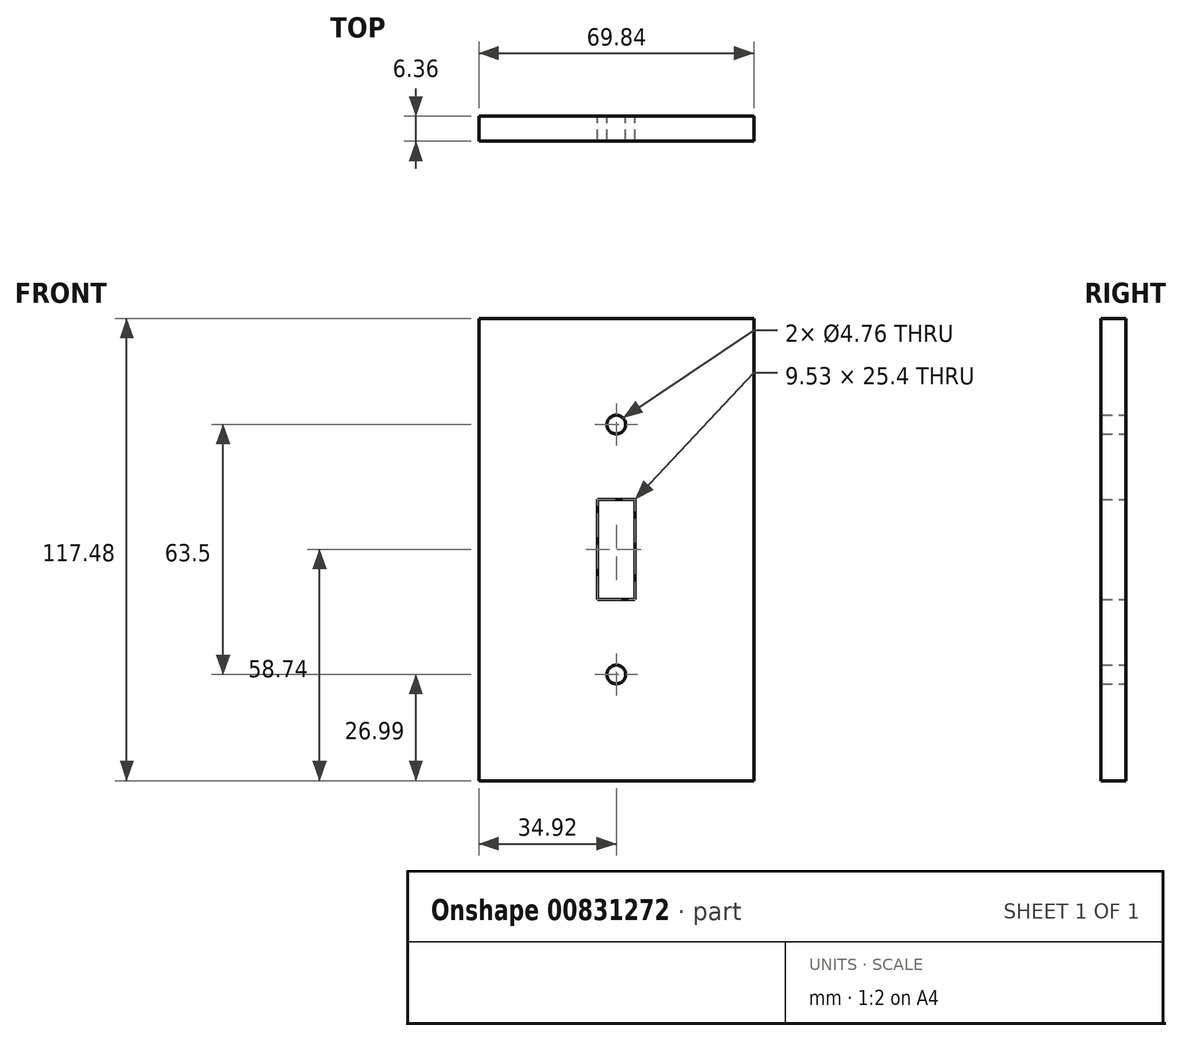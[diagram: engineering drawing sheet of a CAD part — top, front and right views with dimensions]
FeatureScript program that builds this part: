
annotation { "Feature Type Name" : "Feature", "Feature Type Description" : "" }
export const myFeature = defineFeature(function(context is Context, id is Id, definition is map)
    precondition{}
    {
        {
            var Q0;
            Q0=qCreatedBy(makeId("Front.planeOp"),FACE);
            var sketch = newSketch(context, id + "F0", { "sketchPlane" : qUnion([Q0])});
            skLineSegment(sketch, "E0.bottom", {"start": v(-34.92, 58.74) * mm, "end": v(34.93, 58.74) * mm});
            skLineSegment(sketch, "E0.top", {"start": v(-34.93, -58.74) * mm, "end": v(34.92, -58.74) * mm});
            skLineSegment(sketch, "E0.left", {"start": v(-34.92, 58.74) * mm, "end": v(-34.93, -58.74) * mm});
            skLineSegment(sketch, "E0.right", {"start": v(34.93, 58.74) * mm, "end": v(34.92, -58.74) * mm});
            skPoint(sketch, "E0.middle", {"position": v(0, 0) * mm});
            skLineSegment(sketch, "E1.bottom", {"start": v(4.76, 12.7) * mm, "end": v(-4.76, 12.7) * mm});
            skLineSegment(sketch, "E1.top", {"start": v(4.76, -12.7) * mm, "end": v(-4.76, -12.7) * mm});
            skLineSegment(sketch, "E1.left", {"start": v(4.76, 12.7) * mm, "end": v(4.76, -12.7) * mm});
            skLineSegment(sketch, "E1.right", {"start": v(-4.76, 12.7) * mm, "end": v(-4.76, -12.7) * mm});
            skCircle(sketch, "E2", {"center": v(0, 31.75) * mm, "radius": 2.38 * mm});
            skCircle(sketch, "E3", {"center": v(0, -31.75) * mm, "radius": 2.38 * mm});
            skSolve(sketch);
        }
        {
            var Q0;
            Q0=makeQuery(id+"F0.imprint","IMPRINT",FACE,{"disambiguationData":[TD([[makeQuery(id+"F0.imprint","IMPRINT",EDGE,{"derivedFrom":sQuery(id+"F0.wireOp",EDGE,"E0.bottom")}),-1.0]])]});
            extrude(context, id + "F1", {"entities" : qUnion([Q0]), "endBound" : BoundingType.SYMMETRIC, "depth" : 6.35 * mm, "offsetDistance" : 25.4 * mm});
        }
    });
